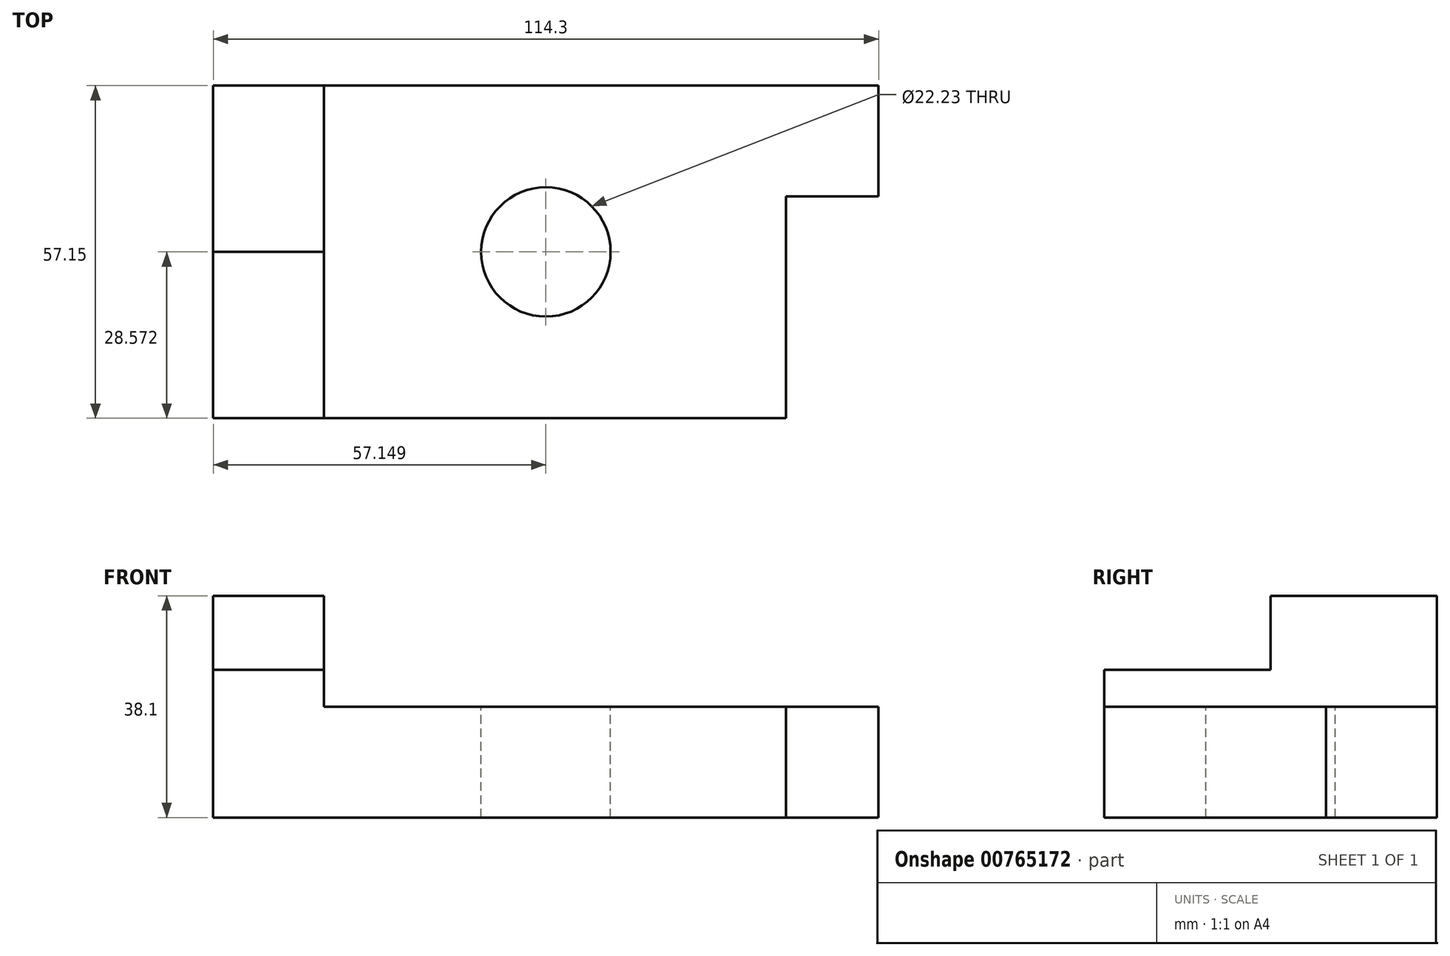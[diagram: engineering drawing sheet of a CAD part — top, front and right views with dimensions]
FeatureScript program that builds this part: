
annotation { "Feature Type Name" : "Feature", "Feature Type Description" : "" }
export const myFeature = defineFeature(function(context is Context, id is Id, definition is map)
    precondition{}
    {
        {
            var Q0;
            Q0=qCreatedBy(makeId("Top.planeOp"),FACE);
            var sketch = newSketch(context, id + "F0", { "sketchPlane" : qUnion([Q0])});
            skLineSegment(sketch, "E0.bottom", {"start": v(-48.03, 25.72) * mm, "end": v(66.27, 25.72) * mm});
            skLineSegment(sketch, "E0.top", {"start": v(-48.03, -31.43) * mm, "end": v(66.27, -31.43) * mm});
            skLineSegment(sketch, "E0.left", {"start": v(-48.03, 25.72) * mm, "end": v(-48.03, -31.43) * mm});
            skLineSegment(sketch, "E0.right", {"start": v(66.27, 25.72) * mm, "end": v(66.27, -31.43) * mm});
            skSolve(sketch);
        }
        {
            var Q0;
            Q0=qSketchRegion(id+"F0",true);
            extrude(context, id + "F1", {"entities" : qUnion([Q0]), "depth" : 19.05 * mm, "offsetDistance" : 25.4 * mm});
        }
        {
            var Q0;
            Q0=makeQuery(id+"F1.opExtrude","CAP_FACE",FACE,{"disambiguationData":[OSD([sQuery(id+"F0.wireOp",EDGE,"E0.bottom"),sQuery(id+"F0.wireOp",EDGE,"E0.top"),sQuery(id+"F0.wireOp",EDGE,"E0.left"),sQuery(id+"F0.wireOp",EDGE,"E0.right")])],"isStart":false});
            var sketch = newSketch(context, id + "F2", { "sketchPlane" : qUnion([Q0])});
            skLineSegment(sketch, "E1.bottom", {"start": v(-48.03, 25.72) * mm, "end": v(-28.98, 25.72) * mm});
            skLineSegment(sketch, "E1.top", {"start": v(-48.03, -2.86) * mm, "end": v(-28.98, -2.86) * mm});
            skLineSegment(sketch, "E1.left", {"start": v(-48.03, 25.72) * mm, "end": v(-48.03, -2.86) * mm});
            skLineSegment(sketch, "E1.right", {"start": v(-28.98, 25.72) * mm, "end": v(-28.98, -2.86) * mm});
            skSolve(sketch);
        }
        {
            var Q0;
            Q0=makeQuery(id+"F2.imprint","IMPRINT",FACE,{"disambiguationData":[TD([[makeQuery(id+"F2.imprint","IMPRINT",EDGE,{"derivedFrom":sQuery(id+"F2.wireOp",EDGE,"E1.bottom")}),-1.0]])]});
            extrude(context, id + "F3", {"entities" : qUnion([Q0]), "operationType" : NewBodyOperationType.ADD, "depth" : 19.05 * mm, "offsetDistance" : 25.4 * mm});
        }
        {
            var Q0;
            Q0=makeQuery(id+"F1.opExtrude","CAP_FACE",FACE,{"disambiguationData":[OSD([sQuery(id+"F0.wireOp",EDGE,"E0.bottom"),sQuery(id+"F0.wireOp",EDGE,"E0.top"),sQuery(id+"F0.wireOp",EDGE,"E0.left"),sQuery(id+"F0.wireOp",EDGE,"E0.right")])],"isStart":false});
            var sketch = newSketch(context, id + "F4", { "sketchPlane" : qUnion([Q0])});
            skLineSegment(sketch, "E2.bottom", {"start": v(-28.98, -31.43) * mm, "end": v(-48.03, -31.43) * mm});
            skLineSegment(sketch, "E2.top", {"start": v(-28.98, -2.86) * mm, "end": v(-48.03, -2.86) * mm});
            skLineSegment(sketch, "E2.left", {"start": v(-28.98, -31.43) * mm, "end": v(-28.98, -2.86) * mm});
            skLineSegment(sketch, "E2.right", {"start": v(-48.03, -31.43) * mm, "end": v(-48.03, -2.86) * mm});
            skSolve(sketch);
        }
        {
            var Q0;
            Q0=qSketchRegion(id+"F4",true);
            extrude(context, id + "F5", {"entities" : qUnion([Q0]), "operationType" : NewBodyOperationType.ADD, "depth" : 6.35 * mm, "offsetDistance" : 25.4 * mm});
        }
        {
            var Q0;
            Q0=makeQuery(id+"F1.opExtrude","CAP_FACE",FACE,{"disambiguationData":[OSD([sQuery(id+"F0.wireOp",EDGE,"E0.bottom"),sQuery(id+"F0.wireOp",EDGE,"E0.top"),sQuery(id+"F0.wireOp",EDGE,"E0.left"),sQuery(id+"F0.wireOp",EDGE,"E0.right")])],"isStart":false});
            var sketch = newSketch(context, id + "F6", { "sketchPlane" : qUnion([Q0])});
            skCircle(sketch, "E3", {"center": v(9.12, -2.86) * mm, "radius": 11.11 * mm});
            skSolve(sketch);
        }
        {
            var Q0;
            Q0=makeQuery(id+"F6.imprint","IMPRINT",FACE,{"disambiguationData":[TD([[makeQuery(id+"F6.imprint","IMPRINT",EDGE,{"derivedFrom":sQuery(id+"F6.wireOp",EDGE,"E3")}),1.0]])]});
            extrude(context, id + "F7", {"entities" : qUnion([Q0]), "operationType" : NewBodyOperationType.REMOVE, "endBound" : BoundingType.THROUGH_ALL, "oppositeDirection" : true, "depth" : 25.4 * mm, "offsetDistance" : 25.4 * mm});
        }
        {
            var Q0;
            Q0=makeQuery(id+"F1.opExtrude","CAP_FACE",FACE,{"disambiguationData":[OSD([sQuery(id+"F0.wireOp",EDGE,"E0.bottom"),sQuery(id+"F0.wireOp",EDGE,"E0.top"),sQuery(id+"F0.wireOp",EDGE,"E0.left"),sQuery(id+"F0.wireOp",EDGE,"E0.right")])],"isStart":false});
            var sketch = newSketch(context, id + "F8", { "sketchPlane" : qUnion([Q0])});
            skLineSegment(sketch, "E4.bottom", {"start": v(66.27, -31.43) * mm, "end": v(50.4, -31.43) * mm});
            skLineSegment(sketch, "E4.top", {"start": v(66.27, 6.67) * mm, "end": v(50.4, 6.67) * mm});
            skLineSegment(sketch, "E4.left", {"start": v(66.27, -31.43) * mm, "end": v(66.27, 6.67) * mm});
            skLineSegment(sketch, "E4.right", {"start": v(50.4, -31.43) * mm, "end": v(50.4, 6.67) * mm});
            skSolve(sketch);
        }
        {
            var Q0;
            Q0=makeQuery(id+"F8.imprint","IMPRINT",FACE,{"disambiguationData":[TD([[makeQuery(id+"F8.imprint","IMPRINT",EDGE,{"derivedFrom":sQuery(id+"F8.wireOp",EDGE,"E4.bottom")}),1.0]])]});
            extrude(context, id + "F9", {"entities" : qUnion([Q0]), "operationType" : NewBodyOperationType.REMOVE, "endBound" : BoundingType.THROUGH_ALL, "oppositeDirection" : true, "depth" : 25.4 * mm, "offsetDistance" : 25.4 * mm});
        }
    });
